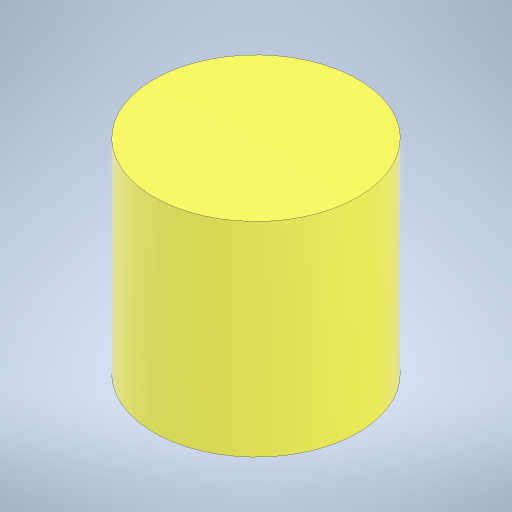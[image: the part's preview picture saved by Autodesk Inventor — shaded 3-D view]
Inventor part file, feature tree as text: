
AUTODESK INVENTOR PART (.ipt)
format: ipt  version: 2024.3 (Build 283343000, 343)  size: 195,584 bytes
history: native  units: mm
features: extrude x1, sketch x1
ambient origin geometry x8: Origin, YZ Plane, XZ Plane, XY Plane, X Axis, Y Axis, Z Axis, Center Point
bodies: Solid1 (feature_tree)
feature tree (2):
  extrude  "Extrusion1"  Depth=4.0mm TaperAngle=0.0deg
  sketch  "Sketch1"  dims[d0=4.0mm d1=4.0mm d2=0.0mm]
